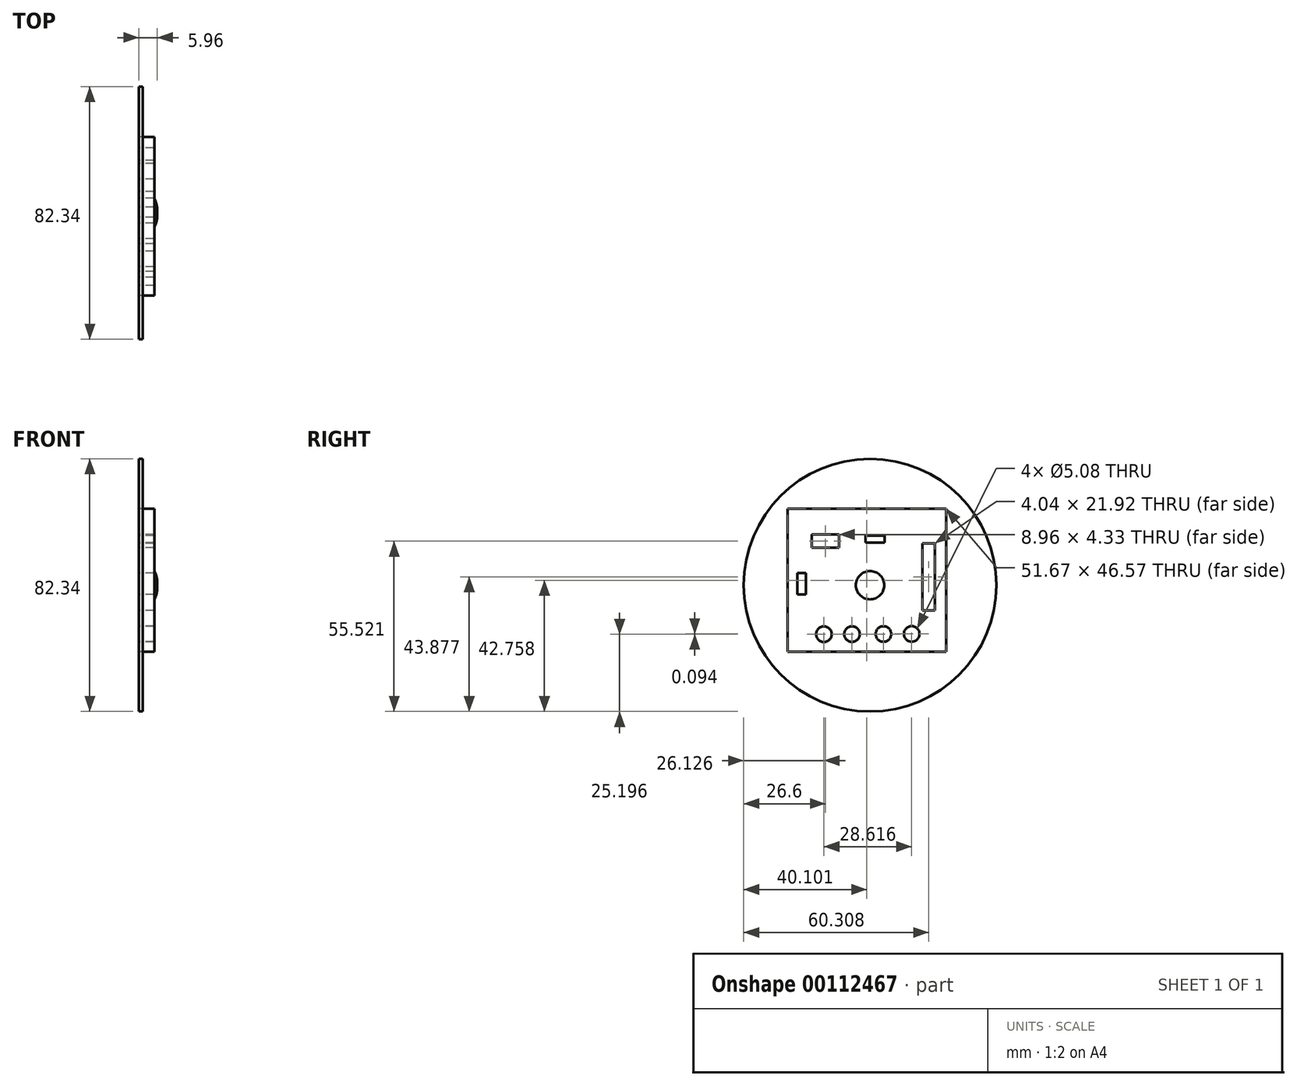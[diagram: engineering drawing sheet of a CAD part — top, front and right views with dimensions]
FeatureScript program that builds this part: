
annotation { "Feature Type Name" : "Feature", "Feature Type Description" : "" }
export const myFeature = defineFeature(function(context is Context, id is Id, definition is map)
    precondition{}
    {
        {
            var Q0;
            Q0=qCreatedBy(makeId("Right.planeOp"),FACE);
            var sketch = newSketch(context, id + "F0", { "sketchPlane" : qUnion([Q0])});
            skCircle(sketch, "E0", {"center": v(0, 0) * mm, "radius": 41.17 * mm});
            skLineSegment(sketch, "E1.bottom", {"start": v(-26.9, 24.87) * mm, "end": v(24.77, 24.87) * mm});
            skLineSegment(sketch, "E1.top", {"start": v(-26.9, -21.7) * mm, "end": v(24.77, -21.7) * mm});
            skLineSegment(sketch, "E1.left", {"start": v(-26.9, 24.87) * mm, "end": v(-26.9, -21.7) * mm});
            skLineSegment(sketch, "E1.right", {"start": v(24.77, 24.87) * mm, "end": v(24.77, -21.7) * mm});
            skLineSegment(sketch, "E2.bottom", {"start": v(-19.05, 16.52) * mm, "end": v(-10.1, 16.52) * mm});
            skLineSegment(sketch, "E2.top", {"start": v(-19.05, 12.19) * mm, "end": v(-10.1, 12.19) * mm});
            skLineSegment(sketch, "E2.left", {"start": v(-19.05, 16.52) * mm, "end": v(-19.05, 12.19) * mm});
            skLineSegment(sketch, "E2.right", {"start": v(-10.1, 16.52) * mm, "end": v(-10.1, 12.19) * mm});
            skLineSegment(sketch, "E3.bottom", {"start": v(-1.45, 16.2) * mm, "end": v(4.77, 16.2) * mm});
            skLineSegment(sketch, "E3.top", {"start": v(-1.45, 13.87) * mm, "end": v(4.77, 13.87) * mm});
            skLineSegment(sketch, "E3.left", {"start": v(-1.45, 16.2) * mm, "end": v(-1.45, 13.87) * mm});
            skLineSegment(sketch, "E3.right", {"start": v(4.77, 16.2) * mm, "end": v(4.77, 13.87) * mm});
            skCircle(sketch, "E4", {"center": v(-5.89, -15.94) * mm, "radius": 2.54 * mm});
            skCircle(sketch, "E5", {"center": v(13.57, -15.88) * mm, "radius": 2.54 * mm});
            skCircle(sketch, "E6", {"center": v(4.37, -15.9) * mm, "radius": 2.54 * mm});
            skCircle(sketch, "E7", {"center": v(-15.04, -15.97) * mm, "radius": 2.54 * mm});
            skLineSegment(sketch, "E8.bottom", {"start": v(17.12, 13.67) * mm, "end": v(21.16, 13.67) * mm});
            skLineSegment(sketch, "E8.top", {"start": v(17.12, -8.25) * mm, "end": v(21.16, -8.25) * mm});
            skLineSegment(sketch, "E8.left", {"start": v(17.12, 13.67) * mm, "end": v(17.12, -8.25) * mm});
            skLineSegment(sketch, "E8.right", {"start": v(21.16, 13.67) * mm, "end": v(21.16, -8.25) * mm});
            skCircle(sketch, "E9", {"center": v(0, 0) * mm, "radius": 4.62 * mm});
            skLineSegment(sketch, "E10.bottom", {"start": v(-23.7, 4.02) * mm, "end": v(-20.96, 4.02) * mm});
            skLineSegment(sketch, "E10.top", {"start": v(-23.7, -3.04) * mm, "end": v(-20.96, -3.04) * mm});
            skLineSegment(sketch, "E10.left", {"start": v(-23.7, 4.02) * mm, "end": v(-23.7, -3.04) * mm});
            skLineSegment(sketch, "E10.right", {"start": v(-20.96, 4.02) * mm, "end": v(-20.96, -3.04) * mm});
            skSolve(sketch);
        }
        {
            var Q0;
            Q0=qCreatedBy(makeId("Right.planeOp"),FACE);
            var sketch = newSketch(context, id + "F1", { "sketchPlane" : qUnion([Q0])});
            skLineSegment(sketch, "E11", {"start": v(0, 41.17) * mm, "end": v(0, -41.17) * mm});
            skSolve(sketch);
        }
        {
            var Q0;
            Q0=qCreatedBy(makeId("Front.planeOp"),FACE);
            var sketch = newSketch(context, id + "F2", { "sketchPlane" : qUnion([Q0])});
            skArc(sketch, "E12", {"start": v(0, 41.17) * mm, "mid": v(-41.17, 0) * mm, "end": v(0, -41.17) * mm});
            skSolve(sketch);
        }
        {
            var Q0;
            Q0=sQuery(id+"F2.wireOp",EDGE,"E12");
            var Q1;
            Q1=sQuery(id+"F1.wireOp",EDGE,"E11");
            revolve(context, id + "F3", {"bodyType" : ToolBodyType.SURFACE, "surfaceEntities" : qUnion([Q0]), "axis" : qUnion([Q1]), "revolveType" : RevolveType.ONE_DIRECTION, "oppositeDirection" : true, "angle" : 90 * degree});
        }
        {
            var Q0;
            Q0=qCreatedBy(makeId("Right.planeOp"),FACE);
            var sketch = newSketch(context, id + "F4", { "sketchPlane" : qUnion([Q0])});
            skLineSegment(sketch, "E13", {"start": v(0, 41.18) * mm, "end": v(0, -41.17) * mm});
            skSolve(sketch);
        }
        {
            var Q0;
            Q0=qCreatedBy(makeId("Front.planeOp"),FACE);
            var sketch = newSketch(context, id + "F5", { "sketchPlane" : qUnion([Q0])});
            skArc(sketch, "E14", {"start": v(0, 41.16) * mm, "mid": v(-41.36, 0) * mm, "end": v(0, -41.16) * mm});
            skSolve(sketch);
        }
        {
            var Q0;
            Q0 = qSketchRegion(id + "F5", true);
            var Q1;
            Q1=sQuery(id+"F5.wireOp",EDGE,"E14");
            var Q2;
            Q2=sQuery(id+"F4.wireOp",EDGE,"E13");
            revolve(context, id + "F6", {"bodyType" : ToolBodyType.SURFACE, "entities" : qUnion([Q0]), "surfaceEntities" : qUnion([Q1]), "axis" : qUnion([Q2]), "revolveType" : RevolveType.ONE_DIRECTION, "angle" : 90 * degree});
        }
        {
            var Q0;
            Q0=makeQuery(id+"F0.imprint","IMPRINT",FACE,{"disambiguationData":[TD([[makeQuery(id+"F0.imprint","IMPRINT",EDGE,{"derivedFrom":sQuery(id+"F0.wireOp",EDGE,"E1.bottom")}),-1.0]])]});
            extrude(context, id + "F7", {"entities" : qUnion([Q0]), "depth" : 5.08 * mm});
        }
        {
            var Q0;
            Q0=makeQuery(id+"F0.imprint","IMPRINT",FACE,{"disambiguationData":[TD([[makeQuery(id+"F0.imprint","IMPRINT",EDGE,{"derivedFrom":sQuery(id+"F0.wireOp",EDGE,"E9")}),1.0]])]});
            extrude(context, id + "F8", {"entities" : qUnion([Q0]), "operationType" : NewBodyOperationType.ADD, "depth" : 5.96 * mm});
        }
        {
            var Q0;
            Q0=makeQuery(id+"F8.opExtrude","CAP_EDGE",EDGE,{"disambiguationData":[OSD([sQuery(id+"F0.wireOp",EDGE,"E9")])],"isStart":false});
            fillet(context, id + "F9", {"entities" : qUnion([Q0]), "radius" : 8.8 * mm, "tangentPropagation" : true, "allowEdgeOverflow" : false});
        }
        {
            var Q0;
            Q0=makeQuery(id+"F0.imprint","IMPRINT",FACE,{"disambiguationData":[TD([[makeQuery(id+"F0.imprint","IMPRINT",EDGE,{"derivedFrom":sQuery(id+"F0.wireOp",EDGE,"E0")}),1.0]])]});
            extrude(context, id + "F10", {"entities" : qUnion([Q0]), "depth" : 1.27 * mm});
        }
    });
